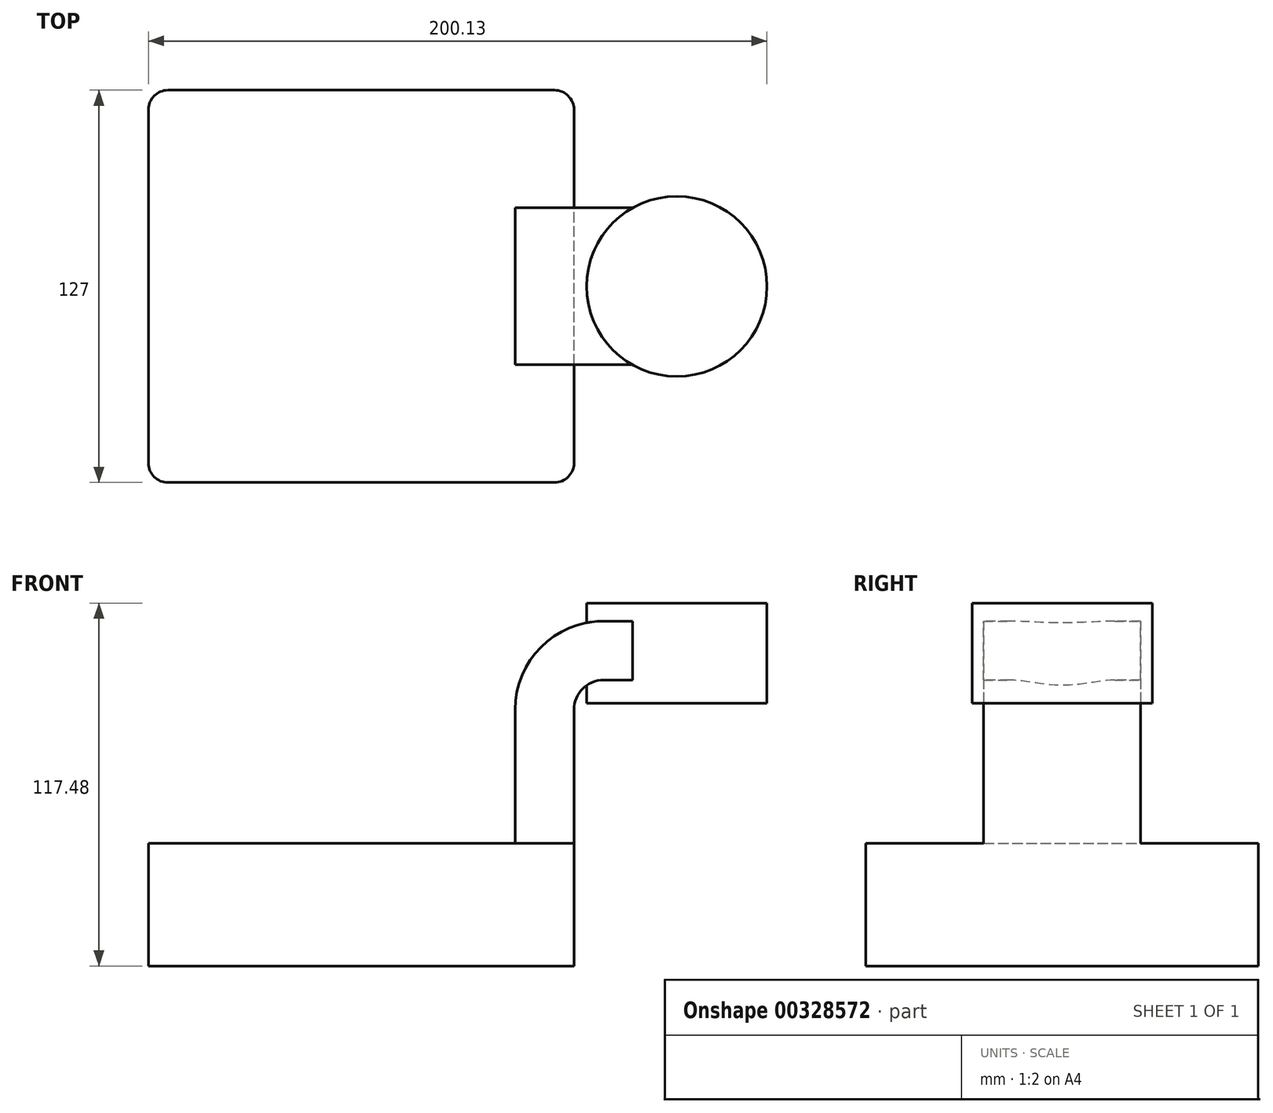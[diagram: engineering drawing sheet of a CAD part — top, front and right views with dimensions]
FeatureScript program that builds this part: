
annotation { "Feature Type Name" : "Feature", "Feature Type Description" : "" }
export const myFeature = defineFeature(function(context is Context, id is Id, definition is map)
    precondition{}
    {
        {
            var Q0;
            Q0=qCreatedBy(makeId("Front.planeOp"),FACE);
            var sketch = newSketch(context, id + "F0", { "sketchPlane" : qUnion([Q0])});
            skLineSegment(sketch, "E0.bottom", {"start": v(-68.85, -19.87) * mm, "end": v(68.85, -19.87) * mm});
            skLineSegment(sketch, "E0.top", {"start": v(-68.85, 19.87) * mm, "end": v(68.85, 19.87) * mm});
            skLineSegment(sketch, "E0.left", {"start": v(-68.85, -19.87) * mm, "end": v(-68.85, 19.87) * mm});
            skLineSegment(sketch, "E0.right", {"start": v(68.85, -19.87) * mm, "end": v(68.85, 19.87) * mm});
            skPoint(sketch, "E0.middle", {"position": v(0, 0) * mm});
            skLineSegment(sketch, "E1.bottom", {"start": v(84.54, 65.15) * mm, "end": v(131.28, 65.15) * mm});
            skLineSegment(sketch, "E1.top", {"start": v(84.54, 97.6) * mm, "end": v(131.28, 97.6) * mm});
            skLineSegment(sketch, "E1.left", {"start": v(84.54, 65.15) * mm, "end": v(84.54, 97.6) * mm});
            skLineSegment(sketch, "E1.right", {"start": v(131.28, 65.15) * mm, "end": v(131.28, 97.6) * mm});
            skLineSegment(sketch, "E2", {"start": v(68.85, 19.87) * mm, "end": v(68.85, 63.1) * mm});
            skLineSegment(sketch, "E3", {"start": v(78.45, 72.7) * mm, "end": v(102.12, 72.7) * mm});
            skArc(sketch, "E4", {"start": v(68.85, 63.1) * mm, "mid": v(71.66, 69.88) * mm, "end": v(78.45, 72.7) * mm});
            skLineSegment(sketch, "E5.0", {"start": v(78.45, 91.74) * mm, "end": v(102.12, 91.74) * mm});
            skArc(sketch, "E5.1", {"start": v(49.8, 63.1) * mm, "mid": v(58.2, 83.35) * mm, "end": v(78.45, 91.74) * mm});
            skLineSegment(sketch, "E5.2", {"start": v(49.8, 19.87) * mm, "end": v(49.8, 63.1) * mm});
            skLineSegment(sketch, "E6", {"start": v(102.12, 91.74) * mm, "end": v(102.12, 72.7) * mm});
            skLineSegment(sketch, "E7", {"start": v(102.12, 97.6) * mm, "end": v(102.12, 65.15) * mm});
            skPoint(sketch, "E7.endSnap0", {"position": v(107.9, 65.15) * mm});
            skFitSpline(sketch, "E8", {"points": [v(-68.85, 19.87) * mm, v(78.45, 91.74) * mm], "startDerivative": vector(0, 122.53) * mm, "endDerivative": vector(148.14, 0) * mm});
            skSolve(sketch);
        }
        {
            var Q0;
            Q0=makeQuery(id+"F0.imprint","IMPRINT",FACE,{"disambiguationData":[TD([[makeQuery(id+"F0.imprint","IMPRINT",EDGE,{"derivedFrom":sQuery(id+"F0.wireOp",EDGE,"E0.bottom")}),1.0]])]});
            extrude(context, id + "F1", {"entities" : qUnion([Q0]), "endBound" : BoundingType.SYMMETRIC, "depth" : 127 * mm});
        }
        {
            var Q0;
            {var subQ4=sQuery(id+"F0.wireOp",EDGE,"E2");Q0=makeQuery(id+"F0.imprint","IMPRINT",FACE,{"disambiguationData":[TD([[makeQuery(id+"F0.imprint","IMPRINT",EDGE,{"derivedFrom":subQ4}),1.0]])]});}
            var Q1;
            {var subQ0=sQuery(id+"F0.wireOp",EDGE,"E3");var subQ1=sQuery(id+"F0.wireOp",EDGE,"E1.left");var subQ2=makeQuery(id+"F0.imprint","INTERSECT",VERTEX,{"derivedFrom":[subQ1,subQ0]});Q1=makeQuery(id+"F0.imprint","IMPRINT",FACE,{"disambiguationData":[TD([[makeQuery(id+"F0.imprint","IMPRINT",EDGE,{"disambiguationData":[TD([[subQ2,-1.0]])],"derivedFrom":subQ1}),-1.0]])]});}
            extrude(context, id + "F2", {"entities" : qUnion([Q0, Q1]), "operationType" : NewBodyOperationType.ADD, "endBound" : BoundingType.SYMMETRIC, "depth" : 50.8 * mm});
        }
        {
            var Q0;
            Q0=makeQuery(id+"F0.imprint","IMPRINT",FACE,{"disambiguationData":[TD([[makeQuery(id+"F0.imprint","IMPRINT",EDGE,{"derivedFrom":sQuery(id+"F0.wireOp",EDGE,"E5.1")}),1.0]])]});
            extrude(context, id + "F3", {"entities" : qUnion([Q0]), "operationType" : NewBodyOperationType.ADD, "endBound" : BoundingType.SYMMETRIC, "depth" : 15.88 * mm});
        }
        {
            var Q0;
            {var subQ0=sQuery(id+"F0.wireOp",EDGE,"E1.right");Q0=makeQuery(id+"F0.imprint","IMPRINT",FACE,{"disambiguationData":[TD([[makeQuery(id+"F0.imprint","IMPRINT",EDGE,{"derivedFrom":subQ0}),1.0]])]});}
            var Q1;
            Q1=sQuery(id+"F0.wireOp",EDGE,"E7");
            revolve(context, id + "F4", {"operationType" : NewBodyOperationType.ADD, "entities" : qUnion([Q0]), "axis" : qUnion([Q1]), "revolveType" : RevolveType.FULL});
        }
        {
            var Q0;
            Q0=makeQuery(id+"F1.opExtrude","CAP_EDGE",EDGE,{"disambiguationData":[OSD([sQuery(id+"F0.wireOp",EDGE,"E0.right")])],"isStart":false});
            var Q1;
            Q1=makeQuery(id+"F1.opExtrude","CAP_EDGE",EDGE,{"disambiguationData":[OSD([sQuery(id+"F0.wireOp",EDGE,"E0.right")])],"isStart":true});
            var Q2;
            Q2=makeQuery(id+"F1.opExtrude","CAP_EDGE",EDGE,{"disambiguationData":[OSD([sQuery(id+"F0.wireOp",EDGE,"E0.left")])],"isStart":false});
            var Q3;
            Q3=makeQuery(id+"F1.opExtrude","CAP_EDGE",EDGE,{"disambiguationData":[OSD([sQuery(id+"F0.wireOp",EDGE,"E0.left")])],"isStart":true});
            fillet(context, id + "F5", {"entities" : qUnion([Q0, Q1, Q2, Q3]), "radius" : 6.35 * mm, "tangentPropagation" : true, "allowEdgeOverflow" : false});
        }
    });
